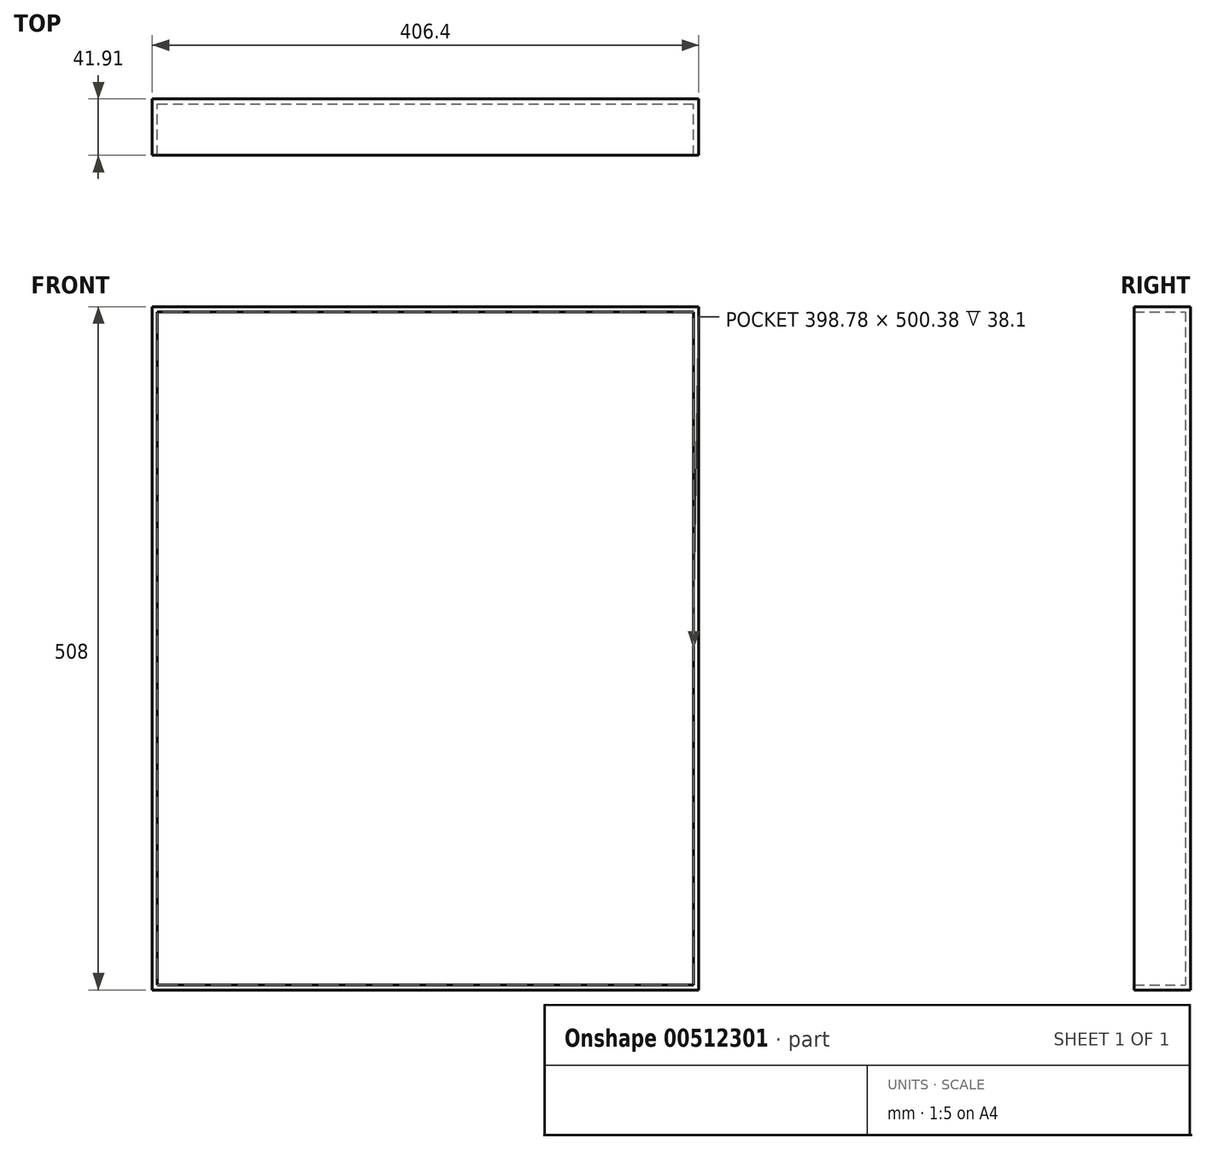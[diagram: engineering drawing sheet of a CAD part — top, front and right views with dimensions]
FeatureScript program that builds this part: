
annotation { "Feature Type Name" : "Feature", "Feature Type Description" : "" }
export const myFeature = defineFeature(function(context is Context, id is Id, definition is map)
    precondition{}
    {
        {
            var Q0;
            Q0=qCreatedBy(makeId("Front.planeOp"),FACE);
            var sketch = newSketch(context, id + "F0", { "sketchPlane" : qUnion([Q0])});
            skLineSegment(sketch, "E0.bottom", {"start": v(-173.22, 278.05) * mm, "end": v(233.18, 278.05) * mm});
            skLineSegment(sketch, "E0.top", {"start": v(-173.22, -229.95) * mm, "end": v(233.18, -229.95) * mm});
            skLineSegment(sketch, "E0.left", {"start": v(-173.22, 278.05) * mm, "end": v(-173.22, -229.95) * mm});
            skLineSegment(sketch, "E0.right", {"start": v(233.18, 278.05) * mm, "end": v(233.18, -229.95) * mm});
            skSolve(sketch);
        }
        {
            var Q0;
            Q0=makeQuery(id+"F0.imprint","IMPRINT",FACE,{"disambiguationData":[TD([[makeQuery(id+"F0.imprint","IMPRINT",EDGE,{"derivedFrom":sQuery(id+"F0.wireOp",EDGE,"E0.bottom")}),-1.0]])]});
            extrude(context, id + "F1", {"entities" : qUnion([Q0]), "depth" : 3.8 * mm});
        }
        {
            var Q0;
            Q0=makeQuery(id+"F1.opExtrude","CAP_FACE",FACE,{"disambiguationData":[OSD([sQuery(id+"F0.wireOp",EDGE,"E0.bottom"),sQuery(id+"F0.wireOp",EDGE,"E0.top"),sQuery(id+"F0.wireOp",EDGE,"E0.left"),sQuery(id+"F0.wireOp",EDGE,"E0.right")])],"isStart":false});
            var sketch = newSketch(context, id + "F2", { "sketchPlane" : qUnion([Q0])});
            skLineSegment(sketch, "E1.bottom", {"start": v(-173.22, 278.05) * mm, "end": v(233.18, 278.05) * mm});
            skLineSegment(sketch, "E1.top", {"start": v(-173.22, -229.95) * mm, "end": v(233.18, -229.95) * mm});
            skLineSegment(sketch, "E1.left", {"start": v(-173.22, 278.05) * mm, "end": v(-173.22, -229.95) * mm});
            skLineSegment(sketch, "E1.right", {"start": v(233.18, 278.05) * mm, "end": v(233.18, -229.95) * mm});
            skLineSegment(sketch, "E2.bottom", {"start": v(-169.4, 274.24) * mm, "end": v(229.37, 274.24) * mm});
            skLineSegment(sketch, "E2.top", {"start": v(-169.4, -226.14) * mm, "end": v(229.37, -226.14) * mm});
            skLineSegment(sketch, "E2.left", {"start": v(-169.4, 274.24) * mm, "end": v(-169.4, -226.14) * mm});
            skLineSegment(sketch, "E2.right", {"start": v(229.37, 274.24) * mm, "end": v(229.37, -226.14) * mm});
            skSolve(sketch);
        }
        {
            var Q0;
            Q0=makeQuery(id+"F2.imprint","IMPRINT",FACE,{"disambiguationData":[TD([[makeQuery(id+"F2.imprint","IMPRINT",EDGE,{"derivedFrom":sQuery(id+"F2.wireOp",EDGE,"E1.bottom")}),-1.0]])]});
            extrude(context, id + "F3", {"entities" : qUnion([Q0]), "operationType" : NewBodyOperationType.ADD, "depth" : 38.1 * mm});
        }
    });
